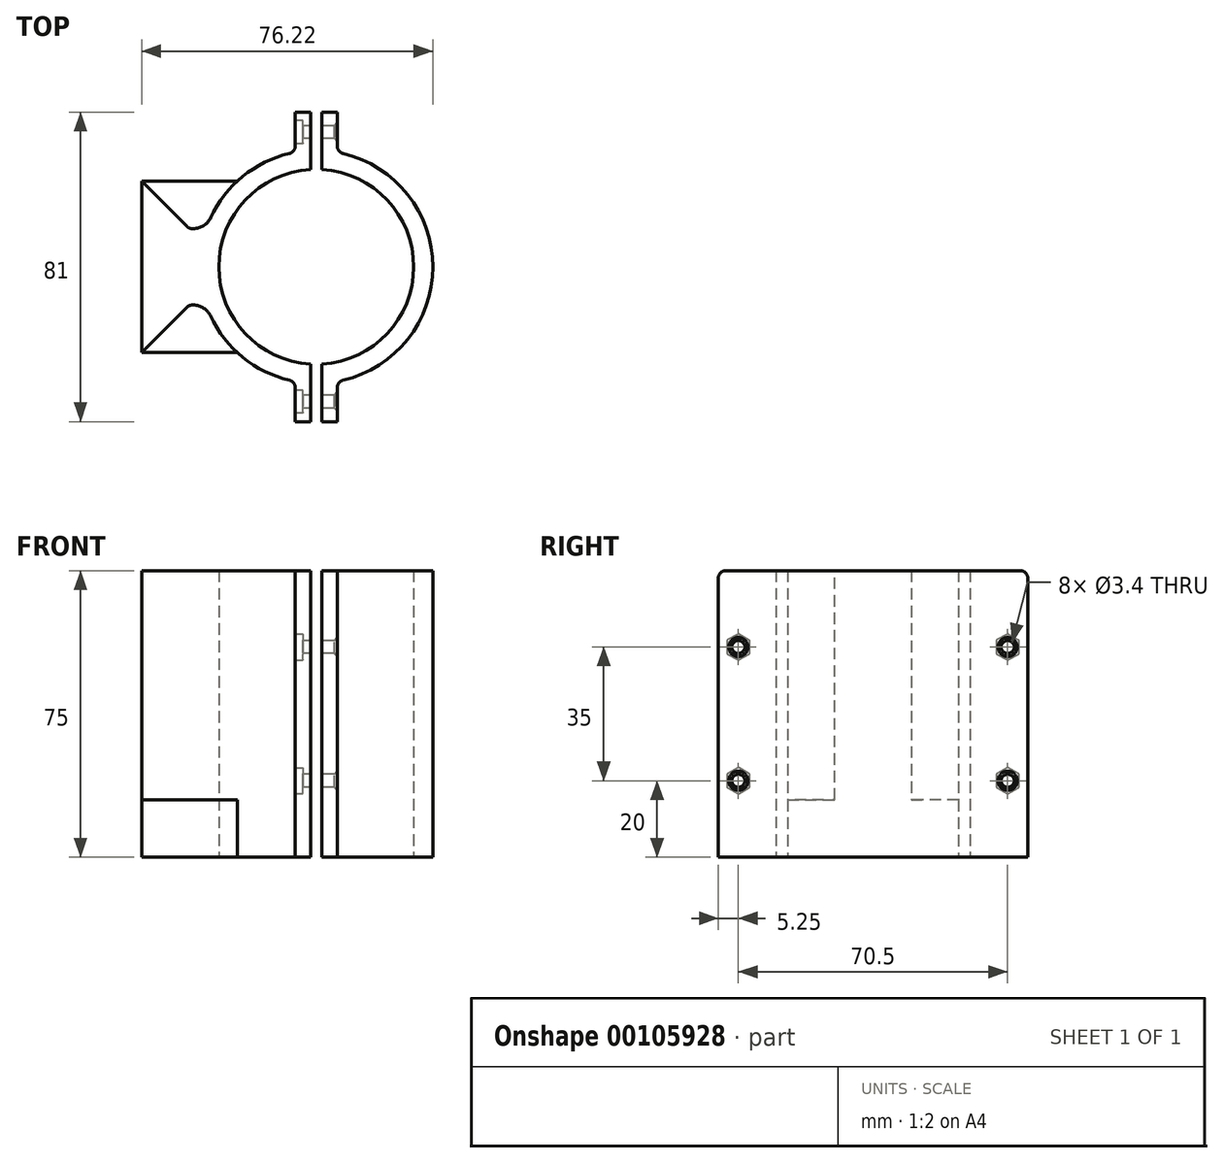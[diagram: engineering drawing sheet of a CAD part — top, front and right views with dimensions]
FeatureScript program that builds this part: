
annotation { "Feature Type Name" : "Feature", "Feature Type Description" : "" }
export const myFeature = defineFeature(function(context is Context, id is Id, definition is map)
    precondition{}
    {
        {
            var Q0;
            Q0=qCreatedBy(makeId("Top.planeOp"),FACE);
            var sketch = newSketch(context, id + "F10", { "sketchPlane" : qUnion([Q0])});
            skLineSegment(sketch, "E0", {"start": v(-5.55, -72.11) * mm, "end": v(110.36, -72.11) * mm, "construction": true});
            skLineSegment(sketch, "E1", {"start": v(-5.55, -72.11) * mm, "end": v(-5.55, -49.71) * mm});
            skLineSegment(sketch, "E2", {"start": v(-5.55, -49.71) * mm, "end": v(6.85, -62.11) * mm});
            skLineSegment(sketch, "E3", {"start": v(6.85, -62.11) * mm, "end": v(11.35, -62.11) * mm});
            skLineSegment(sketch, "E4", {"start": v(11.35, -62.11) * mm, "end": v(11.35, -72.11) * mm});
            skLineSegment(sketch, "E5.MirrorCS", {"start": v(-5.55, -94.51) * mm, "end": v(6.85, -82.11) * mm});
            skLineSegment(sketch, "E6.MirrorCS", {"start": v(11.35, -82.11) * mm, "end": v(11.35, -72.11) * mm});
            skLineSegment(sketch, "E7.MirrorCS", {"start": v(6.85, -82.11) * mm, "end": v(11.35, -82.11) * mm});
            skLineSegment(sketch, "E8.MirrorCS", {"start": v(-5.55, -72.11) * mm, "end": v(-5.55, -94.51) * mm});
            skCircle(sketch, "E9", {"center": v(40.17, -72.11) * mm, "radius": 30.5 * mm});
            skCircle(sketch, "E10.0", {"center": v(40.17, -72.11) * mm, "radius": 25.5 * mm});
            skLineSegment(sketch, "E11", {"start": v(40.17, -31.61) * mm, "end": v(40.17, -110.67) * mm, "construction": true});
            skLineSegment(sketch, "E12", {"start": v(38.67, -31.61) * mm, "end": v(38.67, -46.65) * mm});
            skLineSegment(sketch, "E13", {"start": v(38.67, -31.61) * mm, "end": v(34.67, -31.61) * mm});
            skLineSegment(sketch, "E14", {"start": v(34.67, -31.61) * mm, "end": v(34.67, -47.21) * mm});
            skLineSegment(sketch, "E15.MirrorCS", {"start": v(41.67, -31.61) * mm, "end": v(41.67, -46.65) * mm});
            skLineSegment(sketch, "E16.MirrorCS", {"start": v(45.67, -31.61) * mm, "end": v(45.67, -47.21) * mm});
            skLineSegment(sketch, "E17.MirrorCS", {"start": v(41.67, -31.61) * mm, "end": v(45.67, -31.61) * mm});
            skLineSegment(sketch, "E18.MirrorCS", {"start": v(34.67, -112.61) * mm, "end": v(34.67, -97.01) * mm});
            skLineSegment(sketch, "E19.MirrorCS", {"start": v(41.67, -112.61) * mm, "end": v(45.67, -112.61) * mm});
            skLineSegment(sketch, "E20.MirrorCS", {"start": v(38.67, -112.61) * mm, "end": v(34.67, -112.61) * mm});
            skLineSegment(sketch, "E21.MirrorCS", {"start": v(41.67, -112.61) * mm, "end": v(41.67, -97.57) * mm});
            skLineSegment(sketch, "E22.MirrorCS", {"start": v(45.67, -112.61) * mm, "end": v(45.67, -97.01) * mm});
            skLineSegment(sketch, "E23.MirrorCS", {"start": v(38.67, -112.61) * mm, "end": v(38.67, -97.57) * mm});
            skLineSegment(sketch, "E24", {"start": v(-5.55, -49.71) * mm, "end": v(19.47, -49.71) * mm});
            skLineSegment(sketch, "E25", {"start": v(-5.55, -94.51) * mm, "end": v(19.47, -94.51) * mm});
            skCircle(sketch, "E26", {"center": v(40.17, -31.61) * mm, "radius": 12.5 * mm});
            skCircle(sketch, "E27.MirrorC", {"center": v(40.17, -112.61) * mm, "radius": 12.5 * mm});
            skSolve(sketch);
        }
        {
            var Q0;
            Q0=makeQuery(id+"F10.imprint","IMPRINT",FACE,{"disambiguationData":[TD([[makeQuery(id+"F10.imprint","IMPRINT",EDGE,{"derivedFrom":sQuery(id+"F10.wireOp",EDGE,"E1")}),-1.0]])]});
            var Q1;
            {var subQ0=sQuery(id+"F10.wireOp",EDGE,"E4");Q1=makeQuery(id+"F10.imprint","IMPRINT",FACE,{"disambiguationData":[TD([[makeQuery(id+"F10.imprint","IMPRINT",EDGE,{"derivedFrom":subQ0}),-1.0]])]});}
            var Q2;
            {var subQ10=sQuery(id+"F10.wireOp",EDGE,"E4");Q2=makeQuery(id+"F10.imprint","IMPRINT",FACE,{"disambiguationData":[TD([[makeQuery(id+"F10.imprint","IMPRINT",EDGE,{"derivedFrom":subQ10}),1.0]])]});}
            var Q3;
            {var subQ5=sQuery(id+"F10.wireOp",EDGE,"E13");Q3=makeQuery(id+"F10.imprint","IMPRINT",FACE,{"disambiguationData":[TD([[makeQuery(id+"F10.imprint","IMPRINT",EDGE,{"derivedFrom":subQ5}),1.0]])]});}
            var Q4;
            {var subQ5=sQuery(id+"F10.wireOp",EDGE,"E17.MirrorCS");Q4=makeQuery(id+"F10.imprint","IMPRINT",FACE,{"disambiguationData":[TD([[makeQuery(id+"F10.imprint","IMPRINT",EDGE,{"derivedFrom":subQ5}),-1.0]])]});}
            var Q5;
            {var subQ0=sQuery(id+"F10.wireOp",EDGE,"E12");var subQ3=sQuery(id+"F10.wireOp",EDGE,"E9");var subQ4=makeQuery(id+"F10.imprint","INTERSECT",VERTEX,{"derivedFrom":[subQ3,subQ0]});Q5=makeQuery(id+"F10.imprint","IMPRINT",FACE,{"disambiguationData":[TD([[makeQuery(id+"F10.imprint","IMPRINT",EDGE,{"disambiguationData":[TD([[subQ4,-1.0]])],"derivedFrom":subQ3}),1.0]])]});}
            var Q6;
            {var subQ0=sQuery(id+"F10.wireOp",EDGE,"E16.MirrorCS");var subQ1=sQuery(id+"F10.wireOp",EDGE,"E9");var subQ2=makeQuery(id+"F10.imprint","INTERSECT",VERTEX,{"derivedFrom":[subQ1,subQ0]});Q6=makeQuery(id+"F10.imprint","IMPRINT",FACE,{"disambiguationData":[TD([[makeQuery(id+"F10.imprint","IMPRINT",EDGE,{"disambiguationData":[TD([[subQ2,-1.0]])],"derivedFrom":subQ1}),1.0]])]});}
            var Q7;
            {var subQ0=sQuery(id+"F10.wireOp",EDGE,"E26");var subQ1=sQuery(id+"F10.wireOp",EDGE,"E9");var subQ2=makeQuery(id+"F10.imprint","INTERSECT",VERTEX,{"disambiguationData":[OD(0.0)],"derivedFrom":[subQ1,subQ0]});Q7=makeQuery(id+"F10.imprint","IMPRINT",FACE,{"disambiguationData":[TD([[makeQuery(id+"F10.imprint","IMPRINT",EDGE,{"disambiguationData":[TD([[subQ2,-1.0]])],"derivedFrom":subQ1}),1.0]])]});}
            var Q8;
            {var subQ7=sQuery(id+"F10.wireOp",EDGE,"E26");var subQ9=sQuery(id+"F10.wireOp",EDGE,"E9");var subQ10=makeQuery(id+"F10.imprint","INTERSECT",VERTEX,{"disambiguationData":[OD(0.0)],"derivedFrom":[subQ9,subQ7]});Q8=makeQuery(id+"F10.imprint","IMPRINT",FACE,{"disambiguationData":[TD([[makeQuery(id+"F10.imprint","IMPRINT",EDGE,{"disambiguationData":[TD([[subQ10,1.0]])],"derivedFrom":subQ9}),1.0]])]});}
            var Q9;
            {var subQ0=sQuery(id+"F10.wireOp",EDGE,"E26");var subQ1=sQuery(id+"F10.wireOp",EDGE,"E9");var subQ2=makeQuery(id+"F10.imprint","INTERSECT",VERTEX,{"disambiguationData":[OD(1.0)],"derivedFrom":[subQ1,subQ0]});Q9=makeQuery(id+"F10.imprint","IMPRINT",FACE,{"disambiguationData":[TD([[makeQuery(id+"F10.imprint","IMPRINT",EDGE,{"disambiguationData":[TD([[subQ2,1.0]])],"derivedFrom":subQ1}),1.0]])]});}
            var Q10;
            {var subQ0=sQuery(id+"F10.wireOp",EDGE,"E27.MirrorC");var subQ1=sQuery(id+"F10.wireOp",EDGE,"E9");var subQ2=makeQuery(id+"F10.imprint","INTERSECT",VERTEX,{"disambiguationData":[OD(0.0)],"derivedFrom":[subQ1,subQ0]});Q10=makeQuery(id+"F10.imprint","IMPRINT",FACE,{"disambiguationData":[TD([[makeQuery(id+"F10.imprint","IMPRINT",EDGE,{"disambiguationData":[TD([[subQ2,-1.0]])],"derivedFrom":subQ1}),1.0]])]});}
            var Q11;
            {var subQ3=sQuery(id+"F10.wireOp",EDGE,"E9");var subQ7=sQuery(id+"F10.wireOp",EDGE,"E18.MirrorCS");var subQ9=makeQuery(id+"F10.imprint","INTERSECT",VERTEX,{"derivedFrom":[subQ3,subQ7]});Q11=makeQuery(id+"F10.imprint","IMPRINT",FACE,{"disambiguationData":[TD([[makeQuery(id+"F10.imprint","IMPRINT",EDGE,{"disambiguationData":[TD([[subQ9,-1.0]])],"derivedFrom":subQ3}),1.0]])]});}
            var Q12;
            {var subQ5=sQuery(id+"F10.wireOp",EDGE,"E20.MirrorCS");Q12=makeQuery(id+"F10.imprint","IMPRINT",FACE,{"disambiguationData":[TD([[makeQuery(id+"F10.imprint","IMPRINT",EDGE,{"derivedFrom":subQ5}),-1.0]])]});}
            var Q13;
            {var subQ0=sQuery(id+"F10.wireOp",EDGE,"E27.MirrorC");var subQ1=sQuery(id+"F10.wireOp",EDGE,"E9");var subQ2=makeQuery(id+"F10.imprint","INTERSECT",VERTEX,{"disambiguationData":[OD(1.0)],"derivedFrom":[subQ1,subQ0]});Q13=makeQuery(id+"F10.imprint","IMPRINT",FACE,{"disambiguationData":[TD([[makeQuery(id+"F10.imprint","IMPRINT",EDGE,{"disambiguationData":[TD([[subQ2,1.0]])],"derivedFrom":subQ1}),1.0]])]});}
            var Q14;
            {var subQ1=sQuery(id+"F10.wireOp",EDGE,"E9");var subQ5=sQuery(id+"F10.wireOp",EDGE,"E21.MirrorCS");var subQ8=makeQuery(id+"F10.imprint","INTERSECT",VERTEX,{"derivedFrom":[subQ1,subQ5]});Q14=makeQuery(id+"F10.imprint","IMPRINT",FACE,{"disambiguationData":[TD([[makeQuery(id+"F10.imprint","IMPRINT",EDGE,{"disambiguationData":[TD([[subQ8,-1.0]])],"derivedFrom":subQ1}),1.0]])]});}
            var Q15;
            {var subQ5=sQuery(id+"F10.wireOp",EDGE,"E19.MirrorCS");Q15=makeQuery(id+"F10.imprint","IMPRINT",FACE,{"disambiguationData":[TD([[makeQuery(id+"F10.imprint","IMPRINT",EDGE,{"derivedFrom":subQ5}),1.0]])]});}
            var Q16;
            {var subQ0=sQuery(id+"F10.wireOp",EDGE,"E14");var subQ1=sQuery(id+"F10.wireOp",EDGE,"E10.0");var subQ2=makeQuery(id+"F10.imprint","INTERSECT",VERTEX,{"derivedFrom":[subQ1,subQ0]});Q16=makeQuery(id+"F10.imprint","IMPRINT",FACE,{"disambiguationData":[TD([[makeQuery(id+"F10.imprint","IMPRINT",EDGE,{"disambiguationData":[TD([[subQ2,1.0]])],"derivedFrom":subQ1}),-1.0]])]});}
            var Q17;
            {var subQ0=sQuery(id+"F10.wireOp",EDGE,"E16.MirrorCS");var subQ1=sQuery(id+"F10.wireOp",EDGE,"E10.0");var subQ2=makeQuery(id+"F10.imprint","INTERSECT",VERTEX,{"derivedFrom":[subQ1,subQ0]});Q17=makeQuery(id+"F10.imprint","IMPRINT",FACE,{"disambiguationData":[TD([[makeQuery(id+"F10.imprint","IMPRINT",EDGE,{"disambiguationData":[TD([[subQ2,-1.0]])],"derivedFrom":subQ1}),-1.0]])]});}
            var Q18;
            {var subQ0=sQuery(id+"F10.wireOp",EDGE,"E18.MirrorCS");var subQ1=sQuery(id+"F10.wireOp",EDGE,"E10.0");var subQ2=makeQuery(id+"F10.imprint","INTERSECT",VERTEX,{"derivedFrom":[subQ1,subQ0]});Q18=makeQuery(id+"F10.imprint","IMPRINT",FACE,{"disambiguationData":[TD([[makeQuery(id+"F10.imprint","IMPRINT",EDGE,{"disambiguationData":[TD([[subQ2,-1.0]])],"derivedFrom":subQ1}),-1.0]])]});}
            var Q19;
            {var subQ0=sQuery(id+"F10.wireOp",EDGE,"E22.MirrorCS");var subQ1=sQuery(id+"F10.wireOp",EDGE,"E10.0");var subQ2=makeQuery(id+"F10.imprint","INTERSECT",VERTEX,{"derivedFrom":[subQ1,subQ0]});Q19=makeQuery(id+"F10.imprint","IMPRINT",FACE,{"disambiguationData":[TD([[makeQuery(id+"F10.imprint","IMPRINT",EDGE,{"disambiguationData":[TD([[subQ2,1.0]])],"derivedFrom":subQ1}),-1.0]])]});}
            extrude(context, id + "F0", {"entities" : qUnion([Q0, Q1, Q2, Q3, Q4, Q5, Q6, Q7, Q8, Q9, Q10, Q11, Q12, Q13, Q14, Q15, Q16, Q17, Q18, Q19]), "depth" : 75 * mm});
        }
        {
            var Q0;
            Q0=makeQuery(id+"F10.imprint","IMPRINT",FACE,{"disambiguationData":[TD([[makeQuery(id+"F10.imprint","IMPRINT",EDGE,{"derivedFrom":sQuery(id+"F10.wireOp",EDGE,"E5.MirrorCS")}),-1.0]])]});
            var Q1;
            Q1=makeQuery(id+"F10.imprint","IMPRINT",FACE,{"disambiguationData":[TD([[makeQuery(id+"F10.imprint","IMPRINT",EDGE,{"derivedFrom":sQuery(id+"F10.wireOp",EDGE,"E2")}),1.0]])]});
            extrude(context, id + "F1", {"entities" : qUnion([Q0, Q1]), "operationType" : NewBodyOperationType.ADD, "depth" : 15 * mm});
        }
        {
            var Q0;
            Q0=makeQuery(id+"F0.opExtrude","SWEPT_FACE",FACE,{"disambiguationData":[OSD([sQuery(id+"F10.wireOp",EDGE,"E18.MirrorCS")])]});
            var sketch = newSketch(context, id + "F2", { "sketchPlane" : qUnion([Q0])});
            skLineSegment(sketch, "E28", {"start": v(107.36, 72.5) * mm, "end": v(107.36, 37.5) * mm, "construction": true});
            skLineSegment(sketch, "E29", {"start": v(107.36, 37.5) * mm, "end": v(107.36, 2.5) * mm, "construction": true});
            skCircle(sketch, "E30.cCircle", {"center": v(107.36, 55) * mm, "radius": 3 * mm, "construction": true});
            skLineSegment(sketch, "E30.0", {"start": v(104.36, 53.27) * mm, "end": v(104.36, 56.73) * mm});
            skLineSegment(sketch, "E30.1", {"start": v(104.36, 56.73) * mm, "end": v(107.36, 58.46) * mm});
            skLineSegment(sketch, "E30.2", {"start": v(107.36, 58.46) * mm, "end": v(110.36, 56.73) * mm});
            skLineSegment(sketch, "E30.3", {"start": v(110.36, 56.73) * mm, "end": v(110.36, 53.27) * mm});
            skLineSegment(sketch, "E30.4", {"start": v(110.36, 53.27) * mm, "end": v(107.36, 51.54) * mm});
            skLineSegment(sketch, "E30.5", {"start": v(107.36, 51.54) * mm, "end": v(104.36, 53.27) * mm});
            skPoint(sketch, "E30.0.midPoint", {"position": v(104.36, 55) * mm});
            skCircle(sketch, "E31.cCircle", {"center": v(107.36, 20) * mm, "radius": 3 * mm, "construction": true});
            skLineSegment(sketch, "E31.0", {"start": v(104.36, 18.27) * mm, "end": v(104.36, 21.73) * mm});
            skLineSegment(sketch, "E31.1", {"start": v(104.36, 21.73) * mm, "end": v(107.36, 23.46) * mm});
            skLineSegment(sketch, "E31.2", {"start": v(107.36, 23.46) * mm, "end": v(110.36, 21.73) * mm});
            skLineSegment(sketch, "E31.3", {"start": v(110.36, 21.73) * mm, "end": v(110.36, 18.27) * mm});
            skLineSegment(sketch, "E31.4", {"start": v(110.36, 18.27) * mm, "end": v(107.36, 16.54) * mm});
            skLineSegment(sketch, "E31.5", {"start": v(107.36, 16.54) * mm, "end": v(104.36, 18.27) * mm});
            skPoint(sketch, "E31.0.midPoint", {"position": v(104.36, 20) * mm});
            skCircle(sketch, "E32", {"center": v(107.36, 55) * mm, "radius": 1.7 * mm});
            skCircle(sketch, "E33", {"center": v(107.36, 20) * mm, "radius": 1.7 * mm});
            skLineSegment(sketch, "E34", {"start": v(107.36, 75) * mm, "end": v(107.36, 0) * mm, "construction": true});
            skLineSegment(sketch, "E35.0", {"start": v(114.52, 55) * mm, "end": v(100.2, 55) * mm, "construction": true});
            skLineSegment(sketch, "E36.0", {"start": v(114.01, 20) * mm, "end": v(100.7, 20) * mm, "construction": true});
            skLineSegment(sketch, "E37", {"start": v(36.86, 72.5) * mm, "end": v(36.86, 37.5) * mm, "construction": true});
            skLineSegment(sketch, "E38", {"start": v(36.86, 37.5) * mm, "end": v(36.86, 2.5) * mm, "construction": true});
            skCircle(sketch, "E39.cCircle", {"center": v(36.86, 55) * mm, "radius": 3 * mm, "construction": true});
            skLineSegment(sketch, "E39.0", {"start": v(33.86, 53.27) * mm, "end": v(33.86, 56.73) * mm});
            skLineSegment(sketch, "E39.1", {"start": v(33.86, 56.73) * mm, "end": v(36.86, 58.46) * mm});
            skLineSegment(sketch, "E39.2", {"start": v(36.86, 58.46) * mm, "end": v(39.86, 56.73) * mm});
            skLineSegment(sketch, "E39.3", {"start": v(39.86, 56.73) * mm, "end": v(39.86, 53.27) * mm});
            skLineSegment(sketch, "E39.4", {"start": v(39.86, 53.27) * mm, "end": v(36.86, 51.54) * mm});
            skLineSegment(sketch, "E39.5", {"start": v(36.86, 51.54) * mm, "end": v(33.86, 53.27) * mm});
            skPoint(sketch, "E39.0.midPoint", {"position": v(33.86, 55) * mm});
            skCircle(sketch, "E40.cCircle", {"center": v(36.86, 20) * mm, "radius": 3 * mm, "construction": true});
            skLineSegment(sketch, "E40.0", {"start": v(33.86, 18.27) * mm, "end": v(33.86, 21.73) * mm});
            skLineSegment(sketch, "E40.1", {"start": v(33.86, 21.73) * mm, "end": v(36.86, 23.46) * mm});
            skLineSegment(sketch, "E40.2", {"start": v(36.86, 23.46) * mm, "end": v(39.86, 21.73) * mm});
            skLineSegment(sketch, "E40.3", {"start": v(39.86, 21.73) * mm, "end": v(39.86, 18.27) * mm});
            skLineSegment(sketch, "E40.4", {"start": v(39.86, 18.27) * mm, "end": v(36.86, 16.54) * mm});
            skLineSegment(sketch, "E40.5", {"start": v(36.86, 16.54) * mm, "end": v(33.86, 18.27) * mm});
            skPoint(sketch, "E40.0.midPoint", {"position": v(33.86, 20) * mm});
            skCircle(sketch, "E41", {"center": v(36.86, 55) * mm, "radius": 1.7 * mm});
            skCircle(sketch, "E42", {"center": v(36.86, 20) * mm, "radius": 1.7 * mm});
            skLineSegment(sketch, "E43", {"start": v(36.86, 94.5) * mm, "end": v(36.86, -5.5) * mm, "construction": true});
            skLineSegment(sketch, "E44.0", {"start": v(45.3, 55) * mm, "end": v(28.43, 55) * mm, "construction": true});
            skLineSegment(sketch, "E45.0", {"start": v(43.63, 20) * mm, "end": v(30.1, 20) * mm, "construction": true});
            skLineSegment(sketch, "E46.0", {"start": v(31.61, 70) * mm, "end": v(42.11, 70) * mm, "construction": true});
            skPoint(sketch, "E47", {"position": v(36.86, 70) * mm});
            skSolve(sketch);
        }
        {
            var Q0;
            Q0=qSketchRegion(id+"F2",true);
            extrude(context, id + "F3", {"entities" : qUnion([Q0]), "operationType" : NewBodyOperationType.REMOVE, "oppositeDirection" : true, "depth" : 2 * mm});
        }
        {
            var Q0;
            Q0=makeQuery(id+"F3.boolean.opBoolean","SPLIT",FACE,{"disambiguationData":[TD([makeQuery(id+"F3.opExtrude","SWEPT_FACE",FACE,{"disambiguationData":[OSD([sQuery(id+"F2.wireOp",EDGE,"E41")])]})])],"derivedFrom":makeQuery(id+"F0.opExtrude","SWEPT_FACE",FACE,{"disambiguationData":[OSD([sQuery(id+"F10.wireOp",EDGE,"E14")])]})});
            var Q1;
            Q1=makeQuery(id+"F3.boolean.opBoolean","SPLIT",FACE,{"disambiguationData":[TD([makeQuery(id+"F3.opExtrude","SWEPT_FACE",FACE,{"disambiguationData":[OSD([sQuery(id+"F2.wireOp",EDGE,"E32")])]})])],"derivedFrom":makeQuery(id+"F0.opExtrude","SWEPT_FACE",FACE,{"disambiguationData":[OSD([sQuery(id+"F10.wireOp",EDGE,"E18.MirrorCS")])]})});
            var Q2;
            Q2=makeQuery(id+"F3.boolean.opBoolean","SPLIT",FACE,{"disambiguationData":[TD([makeQuery(id+"F3.opExtrude","SWEPT_FACE",FACE,{"disambiguationData":[OSD([sQuery(id+"F2.wireOp",EDGE,"E33")])]})])],"derivedFrom":makeQuery(id+"F0.opExtrude","SWEPT_FACE",FACE,{"disambiguationData":[OSD([sQuery(id+"F10.wireOp",EDGE,"E18.MirrorCS")])]})});
            var Q3;
            Q3=makeQuery(id+"F3.boolean.opBoolean","SPLIT",FACE,{"disambiguationData":[TD([makeQuery(id+"F3.opExtrude","SWEPT_FACE",FACE,{"disambiguationData":[OSD([sQuery(id+"F2.wireOp",EDGE,"E42")])]})])],"derivedFrom":makeQuery(id+"F0.opExtrude","SWEPT_FACE",FACE,{"disambiguationData":[OSD([sQuery(id+"F10.wireOp",EDGE,"E14")])]})});
            var Q4;
            Q4=makeQuery(id+"F0.opExtrude","SWEPT_FACE",FACE,{"disambiguationData":[OSD([sQuery(id+"F10.wireOp",EDGE,"E16.MirrorCS")])]});
            var Q5;
            Q5=makeQuery(id+"F0.opExtrude","SWEPT_BODY",BODY,{"disambiguationData":[OSD([sQuery(id+"F10.wireOp",EDGE,"E9"),sQuery(id+"F10.wireOp",EDGE,"E10.0"),sQuery(id+"F10.wireOp",EDGE,"E15.MirrorCS"),sQuery(id+"F10.wireOp",EDGE,"E16.MirrorCS"),sQuery(id+"F10.wireOp",EDGE,"E17.MirrorCS"),sQuery(id+"F10.wireOp",EDGE,"E19.MirrorCS"),sQuery(id+"F10.wireOp",EDGE,"E21.MirrorCS"),sQuery(id+"F10.wireOp",EDGE,"E22.MirrorCS")])]});
            extrude(context, id + "F4", {"entities" : qUnion([Q0, Q1, Q2, Q3]), "operationType" : NewBodyOperationType.REMOVE, "endBound" : BoundingType.THROUGH_ALL, "oppositeDirection" : true, "endBoundEntityFace" : qUnion([Q4]), "endBoundEntityBody" : qUnion([Q5]), "depth" : 46.64 * mm});
        }
        {
            var Q0;
            Q0=makeQuery(id+"F4.boolean.opBoolean","INTERSECT",EDGE,{"derivedFrom":[makeQuery(id+"F0.opExtrude","SWEPT_FACE",FACE,{"disambiguationData":[OSD([sQuery(id+"F10.wireOp",EDGE,"E22.MirrorCS")])]}),makeQuery(id+"F4.opExtrude","SWEPT_FACE",FACE,{"disambiguationData":[OSD([sQuery(id+"F2.wireOp",EDGE,"E33")])]})]});
            var Q1;
            Q1=makeQuery(id+"F4.boolean.opBoolean","INTERSECT",EDGE,{"derivedFrom":[makeQuery(id+"F0.opExtrude","SWEPT_FACE",FACE,{"disambiguationData":[OSD([sQuery(id+"F10.wireOp",EDGE,"E22.MirrorCS")])]}),makeQuery(id+"F4.opExtrude","SWEPT_FACE",FACE,{"disambiguationData":[OSD([sQuery(id+"F2.wireOp",EDGE,"E32")])]})]});
            var Q2;
            Q2=makeQuery(id+"F4.boolean.opBoolean","INTERSECT",EDGE,{"derivedFrom":[makeQuery(id+"F0.opExtrude","SWEPT_FACE",FACE,{"disambiguationData":[OSD([sQuery(id+"F10.wireOp",EDGE,"E16.MirrorCS")])]}),makeQuery(id+"F4.opExtrude","SWEPT_FACE",FACE,{"disambiguationData":[OSD([sQuery(id+"F2.wireOp",EDGE,"E41")])]})]});
            var Q3;
            Q3=makeQuery(id+"F4.boolean.opBoolean","INTERSECT",EDGE,{"derivedFrom":[makeQuery(id+"F0.opExtrude","SWEPT_FACE",FACE,{"disambiguationData":[OSD([sQuery(id+"F10.wireOp",EDGE,"E16.MirrorCS")])]}),makeQuery(id+"F4.opExtrude","SWEPT_FACE",FACE,{"disambiguationData":[OSD([sQuery(id+"F2.wireOp",EDGE,"E42")])]})]});
            chamfer(context, id + "F5", {"entities" : qUnion([Q0, Q1, Q2, Q3]), "width" : 0.8 * mm, "tangentPropagation" : true});
        }
        {
            var Q0;
            Q0=makeQuery(id+"F0.opExtrude","SWEPT_EDGE",EDGE,{"disambiguationData":[OSD([sQuery(id+"F10.wireOp",EDGE,"E9"),sQuery(id+"F10.wireOp",EDGE,"E22.MirrorCS")])]});
            var Q1;
            Q1=makeQuery(id+"F0.opExtrude","SWEPT_EDGE",EDGE,{"disambiguationData":[OSD([sQuery(id+"F10.wireOp",EDGE,"E9"),sQuery(id+"F10.wireOp",EDGE,"E16.MirrorCS")])]});
            var Q2;
            Q2=makeQuery(id+"F0.opExtrude","SWEPT_EDGE",EDGE,{"disambiguationData":[OSD([sQuery(id+"F10.wireOp",EDGE,"E9"),sQuery(id+"F10.wireOp",EDGE,"E14")])]});
            var Q3;
            Q3=makeQuery(id+"F0.opExtrude","SWEPT_EDGE",EDGE,{"disambiguationData":[OSD([sQuery(id+"F10.wireOp",EDGE,"E9"),sQuery(id+"F10.wireOp",EDGE,"E18.MirrorCS")])]});
            var Q4;
            Q4=makeQuery(id+"F0.opExtrude","SWEPT_EDGE",EDGE,{"disambiguationData":[OSD([sQuery(id+"F10.wireOp",EDGE,"E5.MirrorCS"),sQuery(id+"F10.wireOp",EDGE,"E7.MirrorCS")])]});
            var Q5;
            Q5=makeQuery(id+"F0.opExtrude","SWEPT_EDGE",EDGE,{"disambiguationData":[OSD([sQuery(id+"F10.wireOp",EDGE,"E2"),sQuery(id+"F10.wireOp",EDGE,"E3")])]});
            fillet(context, id + "F6", {"entities" : qUnion([Q0, Q1, Q2, Q3, Q4, Q5]), "radius" : 2 * mm, "tangentPropagation" : true, "allowEdgeOverflow" : false});
        }
        {
            var Q0;
            Q0=makeQuery(id+"F0.opExtrude","SWEPT_EDGE",EDGE,{"disambiguationData":[OSD([sQuery(id+"F10.wireOp",EDGE,"E3"),sQuery(id+"F10.wireOp",EDGE,"E4"),sQuery(id+"F10.wireOp",EDGE,"E9")])]});
            var Q1;
            Q1=makeQuery(id+"F0.opExtrude","SWEPT_EDGE",EDGE,{"disambiguationData":[OSD([sQuery(id+"F10.wireOp",EDGE,"E6.MirrorCS"),sQuery(id+"F10.wireOp",EDGE,"E7.MirrorCS"),sQuery(id+"F10.wireOp",EDGE,"E9")])]});
            fillet(context, id + "F7", {"entities" : qUnion([Q0, Q1]), "radius" : 5 * mm, "tangentPropagation" : true, "allowEdgeOverflow" : false});
        }
        {
            var Q0;
            Q0=makeQuery(id+"F3.boolean.opBoolean","COPY",EDGE,{"derivedFrom":makeQuery(id+"F3.opExtrude","SWEPT_EDGE",EDGE,{"disambiguationData":[OSD([sQuery(id+"F2.wireOp",EDGE,"E39.0"),sQuery(id+"F2.wireOp",EDGE,"E39.5")])]})});
            var Q1;
            Q1=makeQuery(id+"F3.boolean.opBoolean","COPY",EDGE,{"derivedFrom":makeQuery(id+"F3.opExtrude","SWEPT_EDGE",EDGE,{"disambiguationData":[OSD([sQuery(id+"F2.wireOp",EDGE,"E39.4"),sQuery(id+"F2.wireOp",EDGE,"E39.5")])]})});
            var Q2;
            Q2=makeQuery(id+"F3.boolean.opBoolean","COPY",EDGE,{"derivedFrom":makeQuery(id+"F3.opExtrude","SWEPT_EDGE",EDGE,{"disambiguationData":[OSD([sQuery(id+"F2.wireOp",EDGE,"E39.1"),sQuery(id+"F2.wireOp",EDGE,"E39.2")])]})});
            var Q3;
            Q3=makeQuery(id+"F3.boolean.opBoolean","COPY",EDGE,{"derivedFrom":makeQuery(id+"F3.opExtrude","SWEPT_EDGE",EDGE,{"disambiguationData":[OSD([sQuery(id+"F2.wireOp",EDGE,"E39.2"),sQuery(id+"F2.wireOp",EDGE,"E39.3")])]})});
            var Q4;
            Q4=makeQuery(id+"F3.boolean.opBoolean","COPY",EDGE,{"derivedFrom":makeQuery(id+"F3.opExtrude","SWEPT_EDGE",EDGE,{"disambiguationData":[OSD([sQuery(id+"F2.wireOp",EDGE,"E39.3"),sQuery(id+"F2.wireOp",EDGE,"E39.4")])]})});
            var Q5;
            Q5=makeQuery(id+"F3.boolean.opBoolean","COPY",EDGE,{"derivedFrom":makeQuery(id+"F3.opExtrude","SWEPT_EDGE",EDGE,{"disambiguationData":[OSD([sQuery(id+"F2.wireOp",EDGE,"E39.0"),sQuery(id+"F2.wireOp",EDGE,"E39.1")])]})});
            var Q6;
            Q6=makeQuery(id+"F3.boolean.opBoolean","COPY",EDGE,{"derivedFrom":makeQuery(id+"F3.opExtrude","SWEPT_EDGE",EDGE,{"disambiguationData":[OSD([sQuery(id+"F2.wireOp",EDGE,"E30.0"),sQuery(id+"F2.wireOp",EDGE,"E30.1")])]})});
            var Q7;
            Q7=makeQuery(id+"F3.boolean.opBoolean","COPY",EDGE,{"derivedFrom":makeQuery(id+"F3.opExtrude","SWEPT_EDGE",EDGE,{"disambiguationData":[OSD([sQuery(id+"F2.wireOp",EDGE,"E30.1"),sQuery(id+"F2.wireOp",EDGE,"E30.2")])]})});
            var Q8;
            Q8=makeQuery(id+"F3.boolean.opBoolean","COPY",EDGE,{"derivedFrom":makeQuery(id+"F3.opExtrude","SWEPT_EDGE",EDGE,{"disambiguationData":[OSD([sQuery(id+"F2.wireOp",EDGE,"E30.0"),sQuery(id+"F2.wireOp",EDGE,"E30.5")])]})});
            var Q9;
            Q9=makeQuery(id+"F3.boolean.opBoolean","COPY",EDGE,{"derivedFrom":makeQuery(id+"F3.opExtrude","SWEPT_EDGE",EDGE,{"disambiguationData":[OSD([sQuery(id+"F2.wireOp",EDGE,"E30.4"),sQuery(id+"F2.wireOp",EDGE,"E30.5")])]})});
            var Q10;
            Q10=makeQuery(id+"F3.boolean.opBoolean","COPY",EDGE,{"derivedFrom":makeQuery(id+"F3.opExtrude","SWEPT_EDGE",EDGE,{"disambiguationData":[OSD([sQuery(id+"F2.wireOp",EDGE,"E30.3"),sQuery(id+"F2.wireOp",EDGE,"E30.4")])]})});
            var Q11;
            Q11=makeQuery(id+"F3.boolean.opBoolean","COPY",EDGE,{"derivedFrom":makeQuery(id+"F3.opExtrude","SWEPT_EDGE",EDGE,{"disambiguationData":[OSD([sQuery(id+"F2.wireOp",EDGE,"E30.2"),sQuery(id+"F2.wireOp",EDGE,"E30.3")])]})});
            var Q12;
            Q12=makeQuery(id+"F3.boolean.opBoolean","COPY",EDGE,{"derivedFrom":makeQuery(id+"F3.opExtrude","SWEPT_EDGE",EDGE,{"disambiguationData":[OSD([sQuery(id+"F2.wireOp",EDGE,"E31.0"),sQuery(id+"F2.wireOp",EDGE,"E31.1")])]})});
            var Q13;
            Q13=makeQuery(id+"F3.boolean.opBoolean","COPY",EDGE,{"derivedFrom":makeQuery(id+"F3.opExtrude","SWEPT_EDGE",EDGE,{"disambiguationData":[OSD([sQuery(id+"F2.wireOp",EDGE,"E31.0"),sQuery(id+"F2.wireOp",EDGE,"E31.5")])]})});
            var Q14;
            Q14=makeQuery(id+"F3.boolean.opBoolean","COPY",EDGE,{"derivedFrom":makeQuery(id+"F3.opExtrude","SWEPT_EDGE",EDGE,{"disambiguationData":[OSD([sQuery(id+"F2.wireOp",EDGE,"E31.1"),sQuery(id+"F2.wireOp",EDGE,"E31.2")])]})});
            var Q15;
            Q15=makeQuery(id+"F3.boolean.opBoolean","COPY",EDGE,{"derivedFrom":makeQuery(id+"F3.opExtrude","SWEPT_EDGE",EDGE,{"disambiguationData":[OSD([sQuery(id+"F2.wireOp",EDGE,"E31.2"),sQuery(id+"F2.wireOp",EDGE,"E31.3")])]})});
            var Q16;
            Q16=makeQuery(id+"F3.boolean.opBoolean","COPY",EDGE,{"derivedFrom":makeQuery(id+"F3.opExtrude","SWEPT_EDGE",EDGE,{"disambiguationData":[OSD([sQuery(id+"F2.wireOp",EDGE,"E31.3"),sQuery(id+"F2.wireOp",EDGE,"E31.4")])]})});
            var Q17;
            Q17=makeQuery(id+"F3.boolean.opBoolean","COPY",EDGE,{"derivedFrom":makeQuery(id+"F3.opExtrude","SWEPT_EDGE",EDGE,{"disambiguationData":[OSD([sQuery(id+"F2.wireOp",EDGE,"E31.4"),sQuery(id+"F2.wireOp",EDGE,"E31.5")])]})});
            var Q18;
            Q18=makeQuery(id+"F3.boolean.opBoolean","COPY",EDGE,{"derivedFrom":makeQuery(id+"F3.opExtrude","SWEPT_EDGE",EDGE,{"disambiguationData":[OSD([sQuery(id+"F2.wireOp",EDGE,"E40.4"),sQuery(id+"F2.wireOp",EDGE,"E40.5")])]})});
            var Q19;
            Q19=makeQuery(id+"F3.boolean.opBoolean","COPY",EDGE,{"derivedFrom":makeQuery(id+"F3.opExtrude","SWEPT_EDGE",EDGE,{"disambiguationData":[OSD([sQuery(id+"F2.wireOp",EDGE,"E40.0"),sQuery(id+"F2.wireOp",EDGE,"E40.5")])]})});
            var Q20;
            Q20=makeQuery(id+"F3.boolean.opBoolean","COPY",EDGE,{"derivedFrom":makeQuery(id+"F3.opExtrude","SWEPT_EDGE",EDGE,{"disambiguationData":[OSD([sQuery(id+"F2.wireOp",EDGE,"E40.0"),sQuery(id+"F2.wireOp",EDGE,"E40.1")])]})});
            var Q21;
            Q21=makeQuery(id+"F3.boolean.opBoolean","COPY",EDGE,{"derivedFrom":makeQuery(id+"F3.opExtrude","SWEPT_EDGE",EDGE,{"disambiguationData":[OSD([sQuery(id+"F2.wireOp",EDGE,"E40.1"),sQuery(id+"F2.wireOp",EDGE,"E40.2")])]})});
            var Q22;
            Q22=makeQuery(id+"F3.boolean.opBoolean","COPY",EDGE,{"derivedFrom":makeQuery(id+"F3.opExtrude","SWEPT_EDGE",EDGE,{"disambiguationData":[OSD([sQuery(id+"F2.wireOp",EDGE,"E40.3"),sQuery(id+"F2.wireOp",EDGE,"E40.4")])]})});
            var Q23;
            Q23=makeQuery(id+"F3.boolean.opBoolean","COPY",EDGE,{"derivedFrom":makeQuery(id+"F3.opExtrude","SWEPT_EDGE",EDGE,{"disambiguationData":[OSD([sQuery(id+"F2.wireOp",EDGE,"E40.2"),sQuery(id+"F2.wireOp",EDGE,"E40.3")])]})});
            fillet(context, id + "F8", {"entities" : qUnion([Q0, Q1, Q2, Q3, Q4, Q5, Q6, Q7, Q8, Q9, Q10, Q11, Q12, Q13, Q14, Q15, Q16, Q17, Q18, Q19, Q20, Q21, Q22, Q23]), "radius" : 0.4 * mm, "tangentPropagation" : true, "allowEdgeOverflow" : false});
        }
        {
            var Q0;
            Q0=makeQuery(id+"F0.opExtrude","CAP_EDGE",EDGE,{"disambiguationData":[OSD([sQuery(id+"F10.wireOp",EDGE,"E17.MirrorCS")])],"isStart":false});
            var Q1;
            Q1=makeQuery(id+"F0.opExtrude","CAP_EDGE",EDGE,{"disambiguationData":[OSD([sQuery(id+"F10.wireOp",EDGE,"E13")])],"isStart":false});
            var Q2;
            Q2=makeQuery(id+"F0.opExtrude","CAP_EDGE",EDGE,{"disambiguationData":[OSD([sQuery(id+"F10.wireOp",EDGE,"E20.MirrorCS")])],"isStart":false});
            var Q3;
            Q3=makeQuery(id+"F0.opExtrude","CAP_EDGE",EDGE,{"disambiguationData":[OSD([sQuery(id+"F10.wireOp",EDGE,"E19.MirrorCS")])],"isStart":false});
            fillet(context, id + "F9", {"entities" : qUnion([Q0, Q1, Q2, Q3]), "radius" : 2 * mm, "tangentPropagation" : true, "allowEdgeOverflow" : false});
        }
    });
